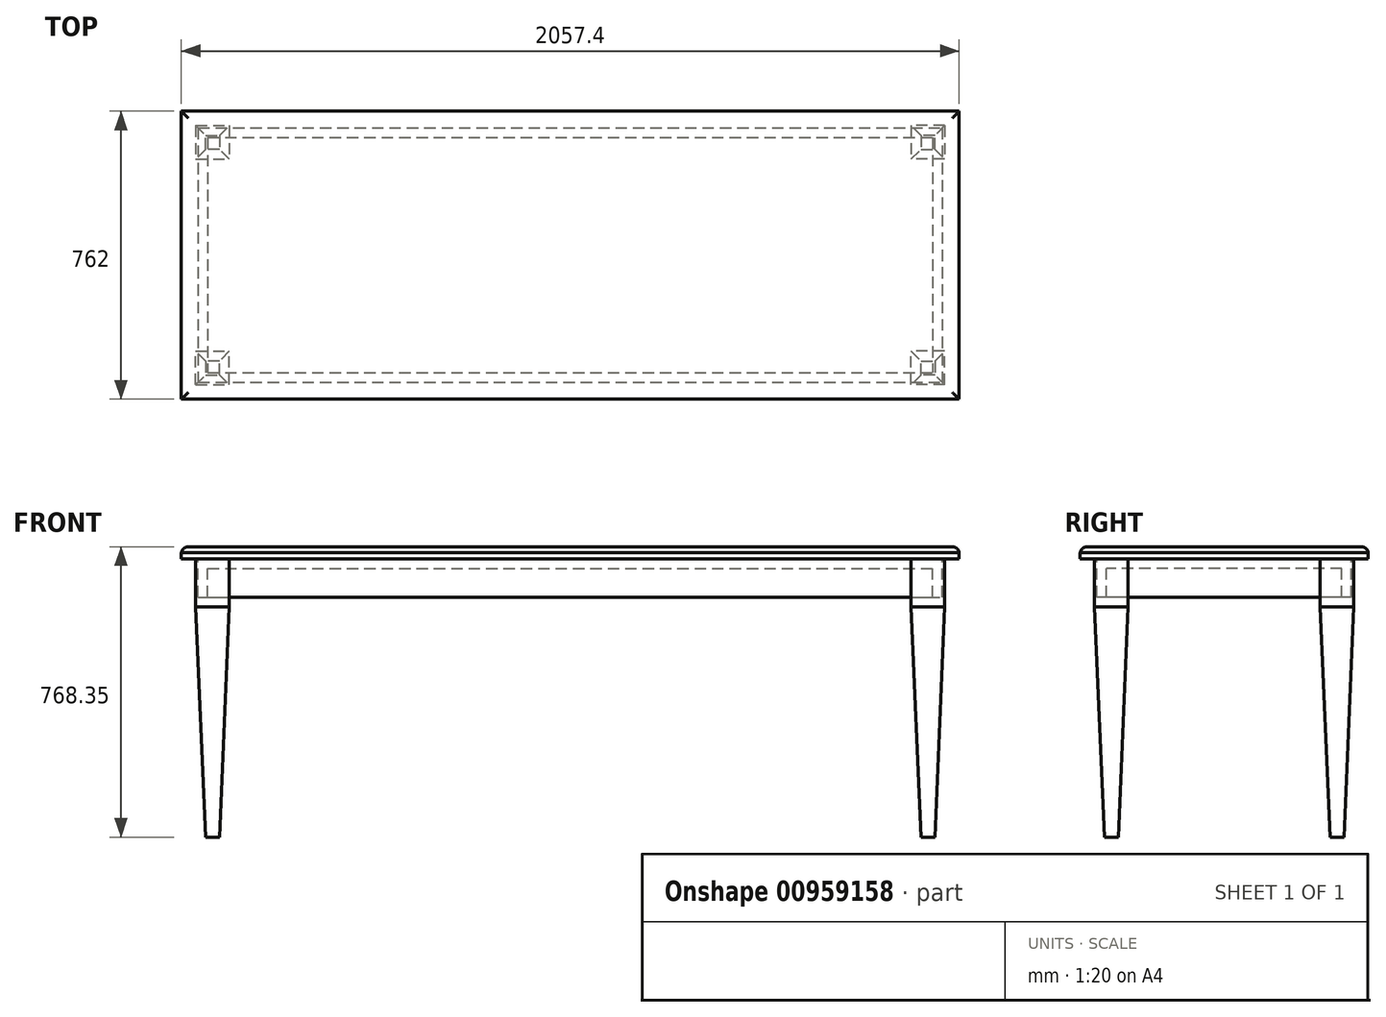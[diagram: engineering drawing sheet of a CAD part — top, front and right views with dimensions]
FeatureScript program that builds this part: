
annotation { "Feature Type Name" : "Feature", "Feature Type Description" : "" }
export const myFeature = defineFeature(function(context is Context, id is Id, definition is map)
    precondition{}
    {
        {
            var Q0;
            Q0=qCreatedBy(makeId("Top.planeOp"),FACE);
            var sketch = newSketch(context, id + "F0", { "sketchPlane" : qUnion([Q0])});
            skLineSegment(sketch, "E0.bottom", {"start": v(-1028.7, 381) * mm, "end": v(1028.7, 381) * mm});
            skLineSegment(sketch, "E0.top", {"start": v(-1028.7, -381) * mm, "end": v(1028.7, -381) * mm});
            skLineSegment(sketch, "E0.left", {"start": v(-1028.7, 381) * mm, "end": v(-1028.7, -381) * mm});
            skLineSegment(sketch, "E0.right", {"start": v(1028.7, 381) * mm, "end": v(1028.7, -381) * mm});
            skPoint(sketch, "E0.middle", {"position": v(0, 0) * mm});
            skSolve(sketch);
        }
        {
            var Q0;
            Q0=qSketchRegion(id+"F0",true);
            extrude(context, id + "F1", {"entities" : qUnion([Q0]), "depth" : 15.88 * mm, "offsetDistance" : 25.4 * mm});
        }
        {
            var Q0;
            Q0=makeQuery(id+"F1.opExtrude","CAP_FACE",FACE,{"disambiguationData":[OSD([sQuery(id+"F0.wireOp",EDGE,"E0.bottom"),sQuery(id+"F0.wireOp",EDGE,"E0.top"),sQuery(id+"F0.wireOp",EDGE,"E0.left"),sQuery(id+"F0.wireOp",EDGE,"E0.right")])],"isStart":false});
            var sketch = newSketch(context, id + "F2", { "sketchPlane" : qUnion([Q0])});
            skLineSegment(sketch, "E1.bottom", {"start": v(-1028.7, 381) * mm, "end": v(1028.7, 381) * mm});
            skLineSegment(sketch, "E1.top", {"start": v(-1028.7, -381) * mm, "end": v(1028.7, -381) * mm});
            skLineSegment(sketch, "E1.left", {"start": v(-1028.7, 381) * mm, "end": v(-1028.7, -381) * mm});
            skLineSegment(sketch, "E1.right", {"start": v(1028.7, 381) * mm, "end": v(1028.7, -381) * mm});
            skPoint(sketch, "E1.middle", {"position": v(0, 0) * mm});
            skSolve(sketch);
        }
        {
            var Q0;
            Q0=qSketchRegion(id+"F2",true);
            extrude(context, id + "F3", {"entities" : qUnion([Q0]), "depth" : 15.88 * mm, "offsetDistance" : 25.4 * mm});
        }
        {
            var Q0;
            Q0=makeQuery(id+"F3.opExtrude","CAP_EDGE",EDGE,{"disambiguationData":[OSD([sQuery(id+"F2.wireOp",EDGE,"E1.top")])],"isStart":false});
            var Q1;
            Q1=makeQuery(id+"F3.opExtrude","CAP_EDGE",EDGE,{"disambiguationData":[OSD([sQuery(id+"F2.wireOp",EDGE,"E1.left")])],"isStart":false});
            var Q2;
            Q2=makeQuery(id+"F3.opExtrude","CAP_EDGE",EDGE,{"disambiguationData":[OSD([sQuery(id+"F2.wireOp",EDGE,"E1.right")])],"isStart":false});
            var Q3;
            Q3=makeQuery(id+"F3.opExtrude","CAP_EDGE",EDGE,{"disambiguationData":[OSD([sQuery(id+"F2.wireOp",EDGE,"E1.bottom")])],"isStart":false});
            fillet(context, id + "F4", {"entities" : qUnion([Q0, Q1, Q2, Q3]), "radius" : 19.05 * mm, "tangentPropagation" : true, "allowEdgeOverflow" : false});
        }
        {
            var Q0;
            Q0=makeQuery(id+"F1.opExtrude","CAP_FACE",FACE,{"disambiguationData":[OSD([sQuery(id+"F0.wireOp",EDGE,"E0.bottom"),sQuery(id+"F0.wireOp",EDGE,"E0.top"),sQuery(id+"F0.wireOp",EDGE,"E0.left"),sQuery(id+"F0.wireOp",EDGE,"E0.right")])],"isStart":true});
            var sketch = newSketch(context, id + "F5", { "sketchPlane" : qUnion([Q0])});
            skLineSegment(sketch, "E2.bottom", {"start": v(-1028.7, -381) * mm, "end": v(1028.7, -381) * mm});
            skLineSegment(sketch, "E2.top", {"start": v(-1028.7, 381) * mm, "end": v(1028.7, 381) * mm});
            skLineSegment(sketch, "E2.left", {"start": v(-1028.7, -381) * mm, "end": v(-1028.7, 381) * mm});
            skLineSegment(sketch, "E2.right", {"start": v(1028.7, -381) * mm, "end": v(1028.7, 381) * mm});
            skPoint(sketch, "E2.middle", {"position": v(0, 0) * mm});
            skLineSegment(sketch, "E3.0", {"start": v(-990.6, -342.9) * mm, "end": v(-990.6, 342.9) * mm});
            skLineSegment(sketch, "E3.1", {"start": v(-990.6, -342.9) * mm, "end": v(990.6, -342.9) * mm});
            skLineSegment(sketch, "E3.2", {"start": v(990.6, -342.9) * mm, "end": v(990.6, 342.9) * mm});
            skLineSegment(sketch, "E3.3", {"start": v(-990.6, 342.9) * mm, "end": v(990.6, 342.9) * mm});
            skLineSegment(sketch, "E4.0", {"start": v(-984.25, 336.55) * mm, "end": v(984.25, 336.55) * mm});
            skLineSegment(sketch, "E4.1", {"start": v(-984.25, -336.55) * mm, "end": v(-984.25, 336.55) * mm});
            skLineSegment(sketch, "E4.2", {"start": v(-984.25, -336.55) * mm, "end": v(984.25, -336.55) * mm});
            skLineSegment(sketch, "E4.3", {"start": v(984.25, -336.55) * mm, "end": v(984.25, 336.55) * mm});
            skLineSegment(sketch, "E5.bottom", {"start": v(-990.6, 342.9) * mm, "end": v(-901.7, 342.9) * mm});
            skLineSegment(sketch, "E5.top", {"start": v(-990.6, 254) * mm, "end": v(-901.7, 254) * mm});
            skLineSegment(sketch, "E5.left", {"start": v(-990.6, 342.9) * mm, "end": v(-990.6, 254) * mm});
            skLineSegment(sketch, "E5.right", {"start": v(-901.7, 342.9) * mm, "end": v(-901.7, 254) * mm});
            skLineSegment(sketch, "E6", {"start": v(-775.87, 0) * mm, "end": v(783.48, 0) * mm, "construction": true});
            skLineSegment(sketch, "E7", {"start": v(0, 524.15) * mm, "end": v(0, -552.6) * mm, "construction": true});
            skLineSegment(sketch, "E8.MirrorCS", {"start": v(-901.7, -342.9) * mm, "end": v(-901.7, -254) * mm});
            skLineSegment(sketch, "E9.MirrorCS", {"start": v(-990.6, -342.9) * mm, "end": v(-901.7, -342.9) * mm});
            skLineSegment(sketch, "E10.MirrorCS", {"start": v(-990.6, -342.9) * mm, "end": v(-990.6, -254) * mm});
            skLineSegment(sketch, "E11.MirrorCS", {"start": v(-990.6, -254) * mm, "end": v(-901.7, -254) * mm});
            skSolve(sketch);
        }
        {
            var Q0;
            {var subQ0=sQuery(id+"F5.wireOp",EDGE,"E4.3");Q0=makeQuery(id+"F5.imprint","IMPRINT",FACE,{"disambiguationData":[TD([[makeQuery(id+"F5.imprint","IMPRINT",EDGE,{"derivedFrom":subQ0}),1.0]])]});}
            var sketch = newSketch(context, id + "F6", { "sketchPlane" : qUnion([Q0])});
            skLineSegment(sketch, "E12.0", {"start": v(-990.6, 342.9) * mm, "end": v(-901.7, 342.9) * mm});
            skLineSegment(sketch, "E13.0", {"start": v(-901.7, 342.9) * mm, "end": v(-901.7, 254) * mm});
            skLineSegment(sketch, "E14.0", {"start": v(-990.6, 342.9) * mm, "end": v(-990.6, 254) * mm});
            skLineSegment(sketch, "E15.0", {"start": v(-990.6, 254) * mm, "end": v(-901.7, 254) * mm});
            skLineSegment(sketch, "E16.0", {"start": v(-990.6, -254) * mm, "end": v(-901.7, -254) * mm});
            skLineSegment(sketch, "E17.0", {"start": v(-901.7, -342.9) * mm, "end": v(-901.7, -254) * mm});
            skLineSegment(sketch, "E18.0", {"start": v(-990.6, -342.9) * mm, "end": v(-901.7, -342.9) * mm});
            skLineSegment(sketch, "E19.0", {"start": v(-990.6, -342.9) * mm, "end": v(-990.6, -254) * mm});
            skSolve(sketch);
        }
        {
            var Q0;
            Q0=qSketchRegion(id+"F6",true);
            extrude(context, id + "F7", {"entities" : qUnion([Q0]), "depth" : 127 * mm, "offsetDistance" : 25.4 * mm});
        }
        {
            var Q0;
            Q0=makeQuery(id+"F7.opExtrude","SWEPT_BODY",BODY,{"disambiguationData":[OSD([sQuery(id+"F6.wireOp",EDGE,"E12.0"),sQuery(id+"F6.wireOp",EDGE,"E13.0"),sQuery(id+"F6.wireOp",EDGE,"E14.0"),sQuery(id+"F6.wireOp",EDGE,"E15.0")])]});
            var Q1;
            Q1=makeQuery(id+"F7.opExtrude","SWEPT_BODY",BODY,{"disambiguationData":[OSD([sQuery(id+"F6.wireOp",EDGE,"E16.0"),sQuery(id+"F6.wireOp",EDGE,"E17.0"),sQuery(id+"F6.wireOp",EDGE,"E18.0"),sQuery(id+"F6.wireOp",EDGE,"E19.0")])]});
            var Q2;
            Q2=qCreatedBy(makeId("Right.planeOp"),FACE);
            mirror(context, id + "F8", {"operationType" : NewBodyOperationType.ADD, "entities" : qUnion([Q0, Q1]), "mirrorPlane" : qUnion([Q2])});
        }
        {
            var Q0;
            {var subQ0=sQuery(id+"F5.wireOp",EDGE,"E4.3");Q0=makeQuery(id+"F5.imprint","IMPRINT",FACE,{"disambiguationData":[TD([[makeQuery(id+"F5.imprint","IMPRINT",EDGE,{"derivedFrom":subQ0}),1.0]])]});}
            var sketch = newSketch(context, id + "F9", { "sketchPlane" : qUnion([Q0])});
            skLineSegment(sketch, "E20.0", {"start": v(-984.25, 336.55) * mm, "end": v(984.25, 336.55) * mm});
            skLineSegment(sketch, "E21.0", {"start": v(-984.25, -336.55) * mm, "end": v(-984.25, 336.55) * mm});
            skLineSegment(sketch, "E22.0", {"start": v(-984.25, -336.55) * mm, "end": v(984.25, -336.55) * mm});
            skLineSegment(sketch, "E23.0", {"start": v(984.25, -336.55) * mm, "end": v(984.25, 336.55) * mm});
            skSolve(sketch);
        }
        {
            var Q0;
            Q0=qSketchRegion(id+"F9",true);
            extrude(context, id + "F10", {"entities" : qUnion([Q0]), "depth" : 101.6 * mm, "offsetDistance" : 25.4 * mm});
        }
        {
            var Q0;
            Q0=makeQuery(id+"F10.opExtrude","CAP_FACE",FACE,{"disambiguationData":[OSD([sQuery(id+"F9.wireOp",EDGE,"E20.0"),sQuery(id+"F9.wireOp",EDGE,"E21.0"),sQuery(id+"F9.wireOp",EDGE,"E22.0"),sQuery(id+"F9.wireOp",EDGE,"E23.0")])],"isStart":false});
            var Q1;
            Q1=makeQuery(id+"F10.opExtrude","SWEPT_BODY",BODY,{"disambiguationData":[OSD([sQuery(id+"F9.wireOp",EDGE,"E20.0"),sQuery(id+"F9.wireOp",EDGE,"E21.0"),sQuery(id+"F9.wireOp",EDGE,"E22.0"),sQuery(id+"F9.wireOp",EDGE,"E23.0")])]});
            shell(context, id + "F11", {"entities" : qUnion([Q0]), "parts" : qUnion([Q1]), "thickness" : 25.4 * mm});
        }
        {
            var Q0;
            Q0=makeQuery(id+"F7.opExtrude","CAP_FACE",FACE,{"disambiguationData":[OSD([sQuery(id+"F6.wireOp",EDGE,"E12.0"),sQuery(id+"F6.wireOp",EDGE,"E13.0"),sQuery(id+"F6.wireOp",EDGE,"E14.0"),sQuery(id+"F6.wireOp",EDGE,"E15.0")])],"isStart":false});
            var sketch = newSketch(context, id + "F12", { "sketchPlane" : qUnion([Q0])});
            skLineSegment(sketch, "E24.0.0", {"start": v(-990.6, 342.9) * mm, "end": v(-990.6, 254) * mm});
            skLineSegment(sketch, "E24.0.1", {"start": v(-990.6, 254) * mm, "end": v(-901.7, 254) * mm});
            skLineSegment(sketch, "E24.0.2", {"start": v(-901.7, 254) * mm, "end": v(-901.7, 342.9) * mm});
            skLineSegment(sketch, "E24.0.3", {"start": v(-901.7, 342.9) * mm, "end": v(-990.6, 342.9) * mm});
            skSolve(sketch);
        }
        {
            var Q0;
            Q0=qSketchRegion(id+"F12",true);
            extrude(context, id + "F13", {"entities" : qUnion([Q0]), "depth" : 609.6 * mm, "offsetDistance" : 25.4 * mm, "hasDraft" : true, "draftAngle" : 2.5 * degree, "draftPullDirection" : true});
        }
        {
            var Q0;
            Q0=makeQuery(id+"F13.opExtrude","SWEPT_BODY",BODY,{"disambiguationData":[OSD([sQuery(id+"F12.wireOp",EDGE,"E24.0.0"),sQuery(id+"F12.wireOp",EDGE,"E24.0.1"),sQuery(id+"F12.wireOp",EDGE,"E24.0.2"),sQuery(id+"F12.wireOp",EDGE,"E24.0.3")])]});
            var Q1;
            Q1=qCreatedBy(makeId("Front.planeOp"),FACE);
            mirror(context, id + "F14", {"entities" : qUnion([Q0]), "mirrorPlane" : qUnion([Q1])});
        }
        {
            var Q0;
            Q0=makeQuery(id+"F13.opExtrude","SWEPT_BODY",BODY,{"disambiguationData":[OSD([sQuery(id+"F12.wireOp",EDGE,"E24.0.0"),sQuery(id+"F12.wireOp",EDGE,"E24.0.1"),sQuery(id+"F12.wireOp",EDGE,"E24.0.2"),sQuery(id+"F12.wireOp",EDGE,"E24.0.3")])]});
            var Q1;
            Q1=makeQuery(id+"F14.opPattern","COPY",BODY,{"derivedFrom":makeQuery(id+"F13.opExtrude","SWEPT_BODY",BODY,{"disambiguationData":[OSD([sQuery(id+"F12.wireOp",EDGE,"E24.0.0"),sQuery(id+"F12.wireOp",EDGE,"E24.0.1"),sQuery(id+"F12.wireOp",EDGE,"E24.0.2"),sQuery(id+"F12.wireOp",EDGE,"E24.0.3")])]}),"instanceName":"1"});
            var Q2;
            Q2=qCreatedBy(makeId("Right.planeOp"),FACE);
            mirror(context, id + "F15", {"operationType" : NewBodyOperationType.ADD, "entities" : qUnion([Q0, Q1]), "mirrorPlane" : qUnion([Q2])});
        }
    });
